# Revit family: LFll-TY2236_Metric
name_source: partatom
category: Sprinklers
units: mm (PartAtom-declared; Revit-internal decimal feet)

## family parameters
Always vertical = Yes
Cut with Voids When Loaded = No
Maintain Annotation Orientation = No
OmniClass Number = 23.65.70.17.11.24
OmniClass Title = Fire Fighting Sprinkler Heads
Part Type = Normal
Room Calculation Point = No
Round Connector Dimension = Use Diameter
Shared = No
Work Plane-Based = No

## types (8) — shared parameters
COBie = Yes
COBie.Component.Name = Sprinklers:Pendent_SIN
COBie.Type = Yes
COBie.Type.AssetType = Fixed
COBie.Type.Category = Pr_70_55_97_84:Sprinklers
COBie.Type.DurationUnit = year
COBie.Type.Manufacturer = Tyco Fire Protection Products
COBie.Type.Material = Brass
COBie.Type.Shape = Cylinder
COBie.Type.Size = 1/2"(DN15)
COBie.Type.WarrantyGuarantorParts = http://tycofsbp.com
Coverage = Standard
Coverage_ = Standard
K-Factor = 70.5202
Manufacturer = Tyco Fire Protection Products
Manufacturer URL = www.tyco-fire.com
Material_ = Brass
Model = LFII
Nominal Diameter 1 = 15 mm
Orifice = Standard
Orifice Size = 11 mm
Outside Diameter 1 = 21 mm
Response = Quick
Response_ = Quick
SIN No = TY2236
Takeout 1 = 57 mm
Technical Data Sheet No = TFP403
zero-valued in all types: COBie.Type.NominalHeight, COBie.Type.NominalLength, COBie.Type.NominalWidth, COBie.Type.ReplacementCost, Default Elevation, Style Id

## per-type parameters (varying)
| type | COBie.Component.Description | COBie.Type.Colour | COBie.Type.Finish | COBie.Type.ModelNumber | COBie.Type.ModelReference | Description | Finish_ | Part No | Temperature Rating |
| LFII Pendent, Fast Response Brass 68°C/155°F 1/2" NPT_51-201-1-155 | LFII Wet Pendent  68.3°C K70.6 DN15 NPT Br | Yellow | Natural Brass | 51-212-1-155 | LFII Wet Pendent  68.3°C K70.6 DN15 NPT Br | LFII Wet Pendent  68.3°C K70.6 DN15 NPT Br | Natural Brass | 51-212-1-155 | 68 °C |
| LFII Pendent, Fast Response Brass 79°C/175°F 1/2" NPT_51-201-1-175 | LFII Wet Pendent  79.4°C K70.6 DN15 NPT Br | Yellow | Natural Brass | 51-212-1-175 | LFII Wet Pendent  79.4°C K70.6 DN15 NPT Br | LFII Wet Pendent  79.4°C K70.6 DN15 NPT Br | Natural Brass | 51-212-1-175 | 79 °C |
| LFII Pendent, Fast Response White 68°C/155°F 1/2" NPT_51-201-3-155 | LFII Wet Pendent  68.3°C K70.6 DN15 NPT Wh9010 | White | Pure White | 51-212-3-155 | LFII Wet Pendent  68.3°C K70.6 DN15 NPT Wh9010 | LFII Wet Pendent  68.3°C K70.6 DN15 NPT Wh9010 | White RAL9010 | 51-212-3-155 | 68 °C |
| LFII Pendent, Fast Response White 79°C/175°F 1/2" NPT_51-201-3-175 | LFII Wet Pendent  68.3°C K70.6 DN15 NPT Wh9010 | White | Pure White | 51-212-3-175 | LFII Wet Pendent  68.3°C K70.6 DN15 NPT Wh9010 | LFII Wet Pendent  68.3°C K70.6 DN15 NPT Wh9010 | White RAL9010 | 51-212-3-175 | 68 °C |
| LFII Pendent, Fast Response White 68°C/155°F 1/2" NPT_51-201-4-155 | LFII Wet Pendent  68.3°C K70.6 DN15 NPT Wh9003 | White | Signal White | 51-212-4-155 | LFII Wet Pendent  68.3°C K70.6 DN15 NPT Wh9003 | LFII Wet Pendent  68.3°C K70.6 DN15 NPT Wh9003 | White RAL9003 | 51-212-4-155 | 68 °C |
| LFII Pendent, Fast Response White 79°C/175°F 1/2" NPT_51-201-4-175 | LFII Wet Pendent  79.4°C K70.6 DN15 NPT Wh9003 | White | Signal White | 51-212-4-175 | LFII Wet Pendent  79.4°C K70.6 DN15 NPT Wh9003 | LFII Wet Pendent  79.4°C K70.6 DN15 NPT Wh9003 | White RAL9003 | 51-212-4-175 | 79 °C |
| LFII Pendent, Fast Response Chrome 68°C/155°F 1/2" NPT_51-201-9-155 | LFII Wet Pendent  68.3°C K70.6 DN15 NPT Chr | Silver | Chrome Plated | 51-212-9-155 | LFII Wet Pendent  68.3°C K70.6 DN15 NPT Chr | LFII Wet Pendent  68.3°C K70.6 DN15 NPT Chr | Chrome Plated | 51-212-9-155 | 68 °C |
| LFII Pendent, Fast Response Chrome 79°C/175°F 1/2" NPT_51-201-9-175 | LFII Wet Pendent  79.4°C K70.6 DN15 NPT Chr | Silver | Chrome Plated | 51-212-9-175 | LFII Wet Pendent  79.4°C K70.6 DN15 NPT Chr | LFII Wet Pendent  79.4°C K70.6 DN15 NPT Chr | Chrome Plated | 51-212-9-175 | 79 °C |

## geometry (parser evidence)
native form markers: Blend x2, Sweep x55
no freeform markers — native parametric forms only
